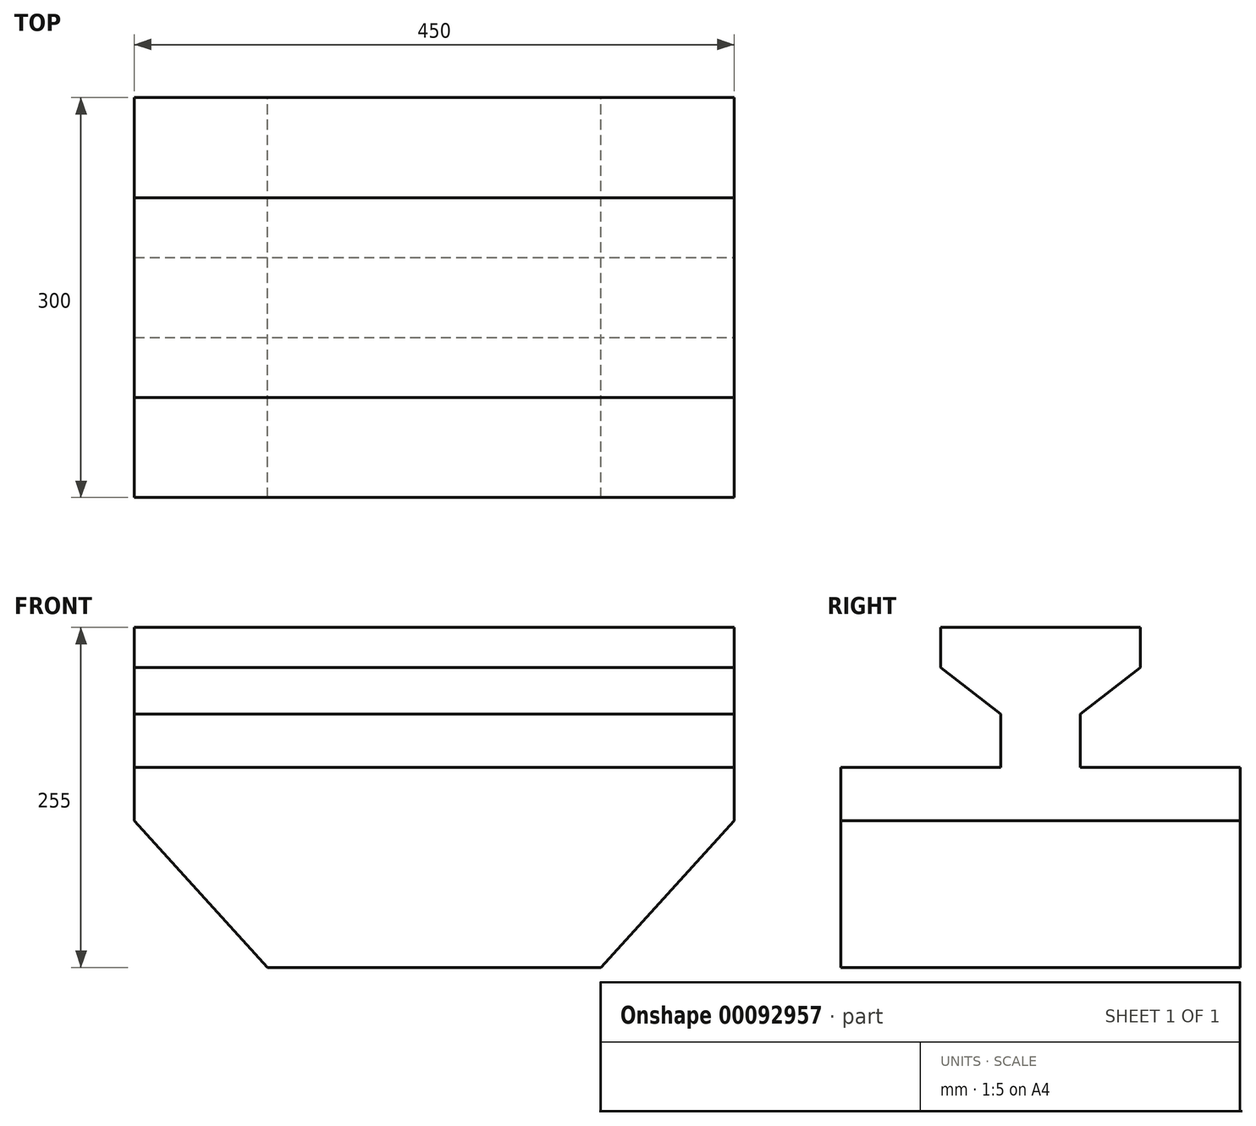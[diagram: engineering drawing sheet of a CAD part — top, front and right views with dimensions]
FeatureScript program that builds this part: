
annotation { "Feature Type Name" : "Feature", "Feature Type Description" : "" }
export const myFeature = defineFeature(function(context is Context, id is Id, definition is map)
    precondition{}
    {
        {
            var Q0;
            Q0=qCreatedBy(makeId("Front.planeOp"),FACE);
            var sketch = newSketch(context, id + "F0", { "sketchPlane" : qUnion([Q0])});
            skLineSegment(sketch, "E0.bottom", {"start": v(225, 75) * mm, "end": v(-225, 75) * mm});
            skLineSegment(sketch, "E0.top", {"start": v(125, -75) * mm, "end": v(-125, -75) * mm});
            skLineSegment(sketch, "E0.left", {"start": v(225, 75) * mm, "end": v(225, 35) * mm});
            skLineSegment(sketch, "E0.right", {"start": v(-225, 75) * mm, "end": v(-225, 35) * mm});
            skPoint(sketch, "E0.middle", {"position": v(0, 0) * mm});
            skLineSegment(sketch, "E1", {"start": v(-225, 35) * mm, "end": v(-125, -75) * mm});
            skLineSegment(sketch, "E2", {"start": v(225, 35) * mm, "end": v(125, -75) * mm});
            skPoint(sketch, "E3.orphan", {"position": v(-225, -75) * mm});
            skPoint(sketch, "E4.orphan", {"position": v(225, -75) * mm});
            skSolve(sketch);
        }
        {
            var Q0;
            Q0 = qSketchRegion(id + "F0", true);
            extrude(context, id + "F1", {"entities" : qUnion([Q0]), "endBound" : BoundingType.SYMMETRIC, "depth" : 300 * mm});
        }
        {
            var Q0;
            Q0=makeQuery(id+"F1.opExtrude","SWEPT_FACE",FACE,{"disambiguationData":[OSD([sQuery(id+"F0.wireOp",EDGE,"E0.left")])]});
            var sketch = newSketch(context, id + "F2", { "sketchPlane" : qUnion([Q0])});
            skLineSegment(sketch, "E5", {"start": v(-30, 75) * mm, "end": v(-30, 115) * mm});
            skLineSegment(sketch, "E6", {"start": v(-30, 115) * mm, "end": v(-75, 150) * mm});
            skLineSegment(sketch, "E7", {"start": v(-75, 150) * mm, "end": v(-75, 180) * mm});
            skLineSegment(sketch, "E8", {"start": v(-75, 180) * mm, "end": v(75, 180) * mm});
            skLineSegment(sketch, "E9", {"start": v(75, 180) * mm, "end": v(75, 150) * mm});
            skLineSegment(sketch, "E10", {"start": v(75, 150) * mm, "end": v(30, 115) * mm});
            skLineSegment(sketch, "E11", {"start": v(30, 115) * mm, "end": v(30, 75) * mm});
            skLineSegment(sketch, "E12", {"start": v(30, 75) * mm, "end": v(-30, 75) * mm});
            skPoint(sketch, "E13", {"position": v(0, 75) * mm});
            skPoint(sketch, "E14", {"position": v(0, 180) * mm});
            skSolve(sketch);
        }
        {
            var Q0;
            Q0 = qSketchRegion(id + "F2", true);
            var Q1;
            Q1=makeQuery(id+"F1.opExtrude","SWEPT_FACE",FACE,{"disambiguationData":[OSD([sQuery(id+"F0.wireOp",EDGE,"E0.right")])]});
            extrude(context, id + "F3", {"entities" : qUnion([Q0]), "operationType" : NewBodyOperationType.ADD, "endBound" : BoundingType.UP_TO_SURFACE, "oppositeDirection" : true, "endBoundEntityFace" : qUnion([Q1]), "depth" : 25 * mm});
        }
    });
